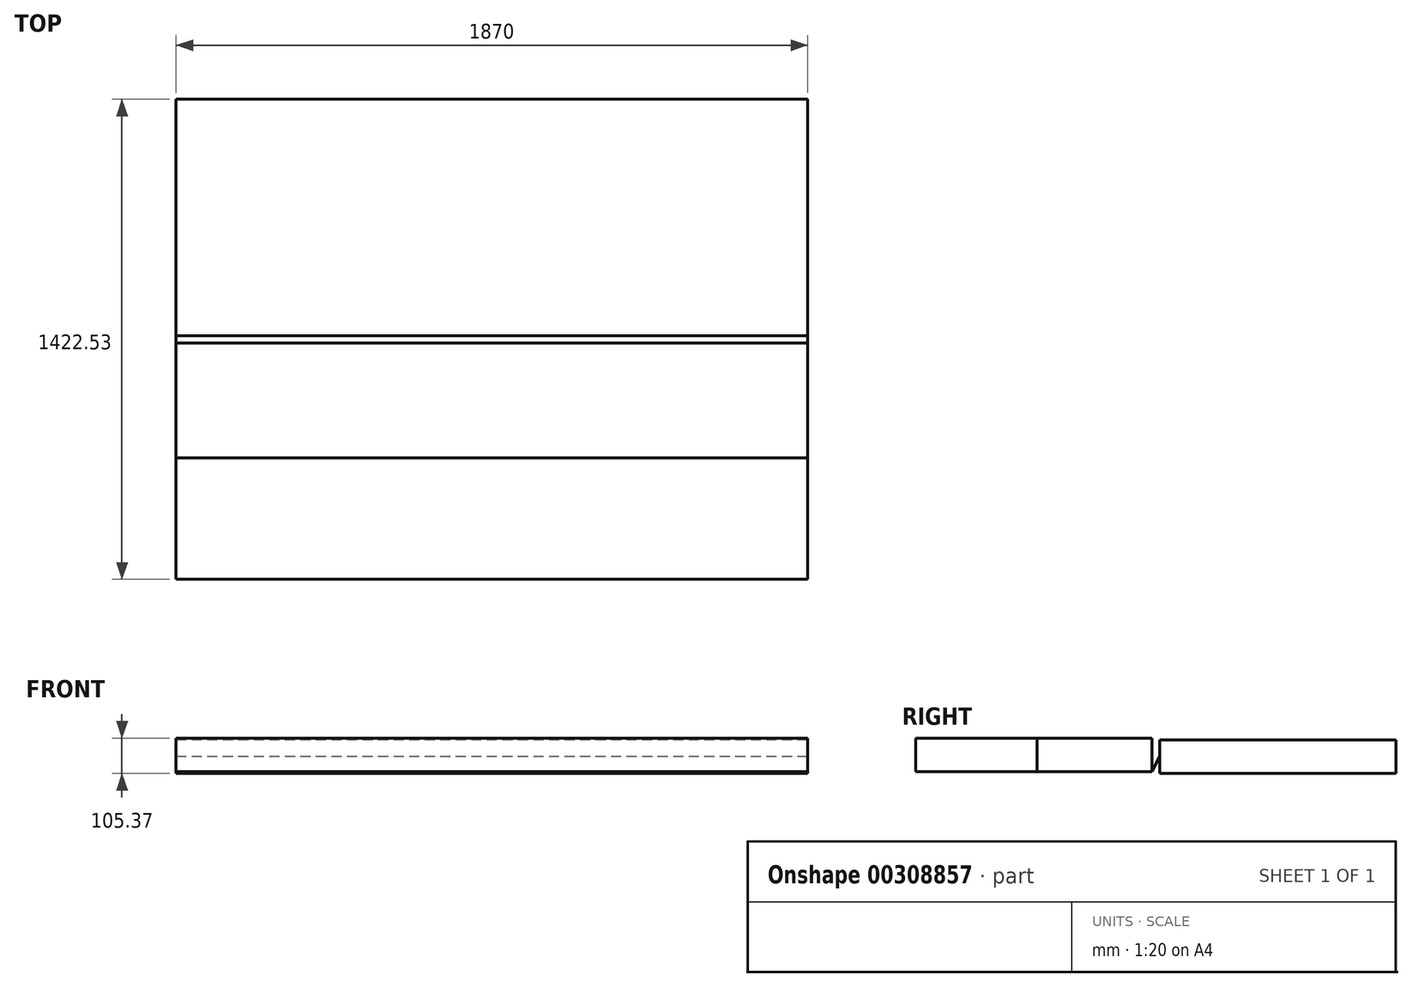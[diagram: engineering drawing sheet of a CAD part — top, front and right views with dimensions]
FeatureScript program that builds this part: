
annotation { "Feature Type Name" : "Feature", "Feature Type Description" : "" }
export const myFeature = defineFeature(function(context is Context, id is Id, definition is map)
    precondition{}
    {
        {
            var Q0;
            Q0=qCreatedBy(makeId("Right.planeOp"),FACE);
            var sketch = newSketch(context, id + "F0", { "sketchPlane" : qUnion([Q0])});
            skLineSegment(sketch, "E0.bottom", {"start": v(-1205.94, 14.65) * mm, "end": v(-845.94, 14.65) * mm});
            skLineSegment(sketch, "E0.top", {"start": v(-1205.94, -85.35) * mm, "end": v(-845.94, -85.35) * mm});
            skLineSegment(sketch, "E0.left", {"start": v(-1205.94, 14.65) * mm, "end": v(-1205.94, -85.35) * mm});
            skLineSegment(sketch, "E0.right", {"start": v(-845.94, 14.65) * mm, "end": v(-845.94, -85.35) * mm});
            skLineSegment(sketch, "E1.bottom", {"start": v(-845.94, 14.65) * mm, "end": v(-505.94, 14.65) * mm});
            skLineSegment(sketch, "E1.top", {"start": v(-845.94, -85.35) * mm, "end": v(-505.94, -85.35) * mm});
            skLineSegment(sketch, "E1.right", {"start": v(-505.94, 14.65) * mm, "end": v(-505.94, -85.35) * mm});
            skLineSegment(sketch, "E2.bottom", {"start": v(-483.41, 9.28) * mm, "end": v(216.59, 9.28) * mm});
            skLineSegment(sketch, "E2.top", {"start": v(-483.41, -90.72) * mm, "end": v(216.59, -90.72) * mm});
            skLineSegment(sketch, "E2.left", {"start": v(-483.41, 9.28) * mm, "end": v(-483.41, -90.72) * mm});
            skLineSegment(sketch, "E2.right", {"start": v(216.59, 9.28) * mm, "end": v(216.59, -90.72) * mm});
            skLineSegment(sketch, "E3", {"start": v(-505.94, -85.35) * mm, "end": v(-483.41, -40.72) * mm});
            skLineSegment(sketch, "E4", {"start": v(-483.41, -40.72) * mm, "end": v(-483.86, -40.5) * mm});
            skLineSegment(sketch, "E5", {"start": v(-483.86, -40.5) * mm, "end": v(-506.06, -84.48) * mm});
            skLineSegment(sketch, "E6", {"start": v(-506.06, -84.48) * mm, "end": v(-505.94, -85.35) * mm});
            skSolve(sketch);
        }
        {
            var Q0;
            Q0=makeQuery(id+"F0.imprint","IMPRINT",FACE,{"disambiguationData":[TD([[makeQuery(id+"F0.imprint","IMPRINT",EDGE,{"derivedFrom":sQuery(id+"F0.wireOp",EDGE,"E0.bottom")}),-1.0]])]});
            extrude(context, id + "F1", {"entities" : qUnion([Q0]), "depth" : 1870 * mm});
        }
        {
            var Q0;
            Q0=makeQuery(id+"F0.imprint","IMPRINT",FACE,{"disambiguationData":[TD([[makeQuery(id+"F0.imprint","IMPRINT",EDGE,{"derivedFrom":sQuery(id+"F0.wireOp",EDGE,"E1.bottom")}),-1.0]])]});
            extrude(context, id + "F2", {"entities" : qUnion([Q0]), "depth" : 1870 * mm});
        }
        {
            var Q0;
            Q0=makeQuery(id+"F0.imprint","IMPRINT",FACE,{"disambiguationData":[TD([[makeQuery(id+"F0.imprint","IMPRINT",EDGE,{"derivedFrom":sQuery(id+"F0.wireOp",EDGE,"E2.bottom")}),-1.0]])]});
            extrude(context, id + "F3", {"entities" : qUnion([Q0]), "depth" : 1870 * mm});
        }
        {
            var Q0;
            {var subQ0=sQuery(id+"F0.wireOp",EDGE,"E3");Q0=makeQuery(id+"F0.imprint","IMPRINT",FACE,{"disambiguationData":[TD([[makeQuery(id+"F0.imprint","IMPRINT",EDGE,{"derivedFrom":subQ0}),1.0]])]});}
            extrude(context, id + "F4", {"entities" : qUnion([Q0]), "depth" : 1870 * mm});
        }
    });
